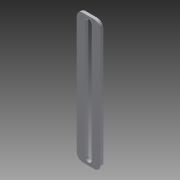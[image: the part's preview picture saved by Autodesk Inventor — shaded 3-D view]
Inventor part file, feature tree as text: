
AUTODESK INVENTOR PART (.ipt)
format: ipt  version: 2013 (Build 170138000, 138)  size: 98,816 bytes
history: native  units: in
note: dims shown in document units (in); Inventor stores cm internally (conversion verified against a paired STEP export)
features: sheet_metal_op x1, chamfer x1, sketch x1, other x1
ambient origin geometry x8: Origin, YZ Plane, XZ Plane, XY Plane, X Axis, Y Axis, Z Axis, Center Point
bodies: Solid1 (feature_tree)
feature tree (4):
  sheet_metal_op  "Face1"
  chamfer  "Corner Round1"
  sketch  "Sketch1"  dims[d0=1.0in d1=0.125in d2=5.5in d4=0.25in d5=0.25in d6=0.25in d7=0.133in d8=0.266in d9=0.133in]
  other  "Plate1"
